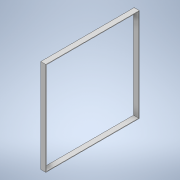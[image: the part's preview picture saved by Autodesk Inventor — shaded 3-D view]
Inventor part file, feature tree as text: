
AUTODESK INVENTOR PART (.ipt)
format: ipt  version: 2020 (Build 240168000, 168)  size: 104,448 bytes
history: native  units: mm
features: extrude x1, sketch x1
ambient origin geometry x8: Origin, YZ Plane, XZ Plane, XY Plane, X Axis, Y Axis, Z Axis, Center Point
bodies: Solid1 (feature_tree)
feature tree (2):
  extrude  "Extrusion1"  Depth=180.0mm
  sketch  "Sketch1"  dims[d0=180.0mm d1=180.0mm d2=90.0mm d3=90.0mm d4=1.0mm d5=1.0mm d6=1.0mm d7=1.0mm d8=10.0mm d9=0.0mm]
